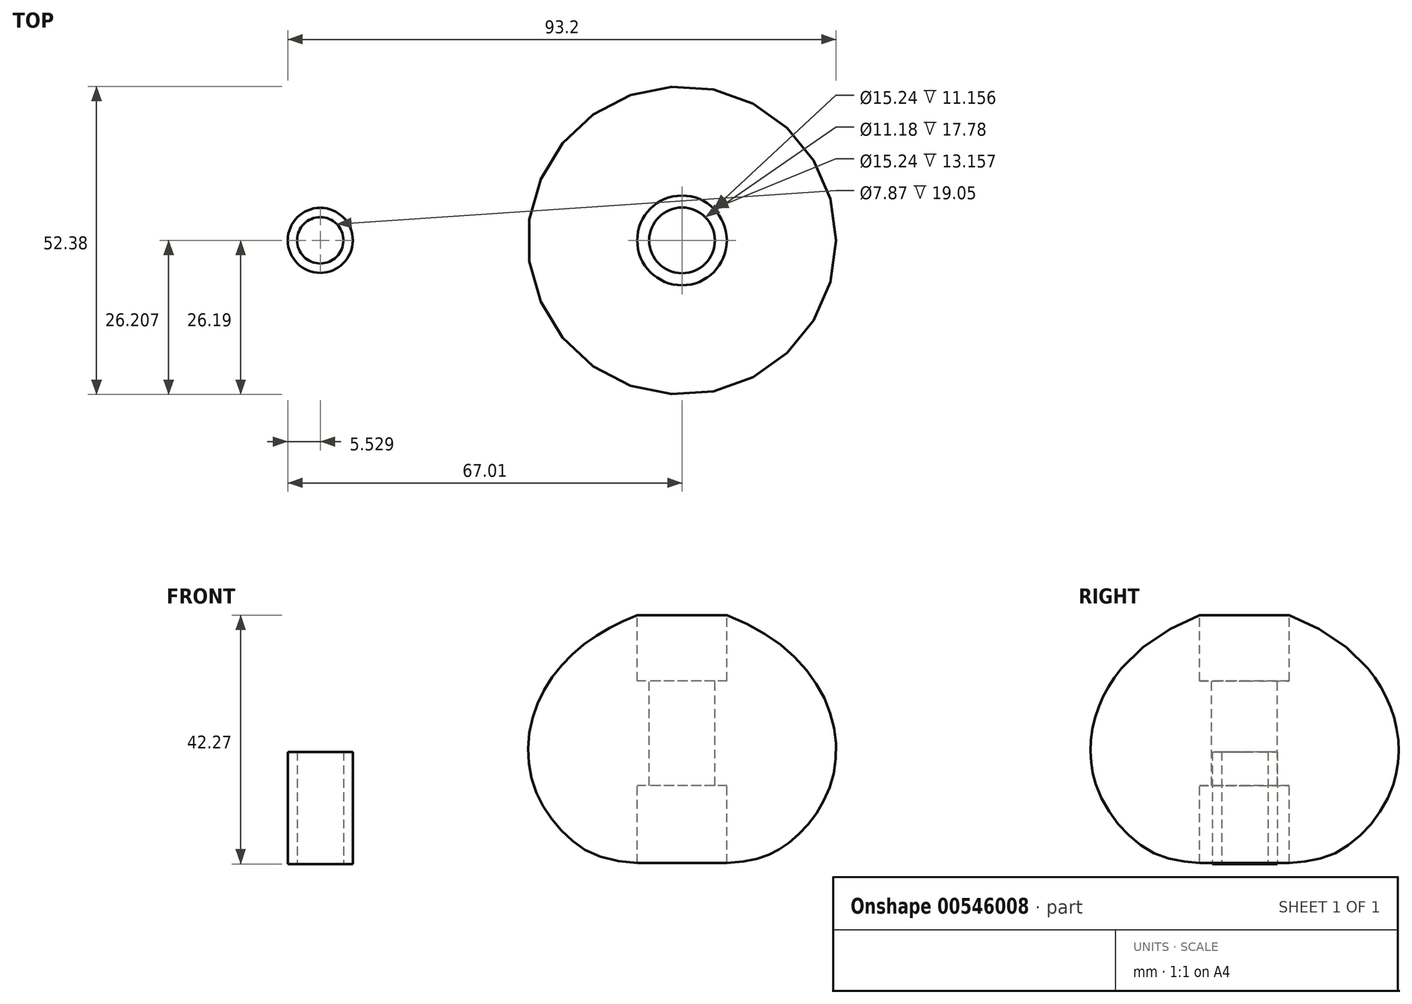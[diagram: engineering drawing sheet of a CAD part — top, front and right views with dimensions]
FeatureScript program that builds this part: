
annotation { "Feature Type Name" : "Feature", "Feature Type Description" : "" }
export const myFeature = defineFeature(function(context is Context, id is Id, definition is map)
    precondition{}
    {
        {
            var Q0;
            Q0=qCreatedBy(makeId("Top.planeOp"),FACE);
            var sketch = newSketch(context, id + "F0", { "sketchPlane" : qUnion([Q0])});
            skCircle(sketch, "E0", {"center": v(-115.86, 6.7) * mm, "radius": 3.94 * mm});
            skCircle(sketch, "E1", {"center": v(-115.86, 6.7) * mm, "radius": 5.52 * mm});
            skSolve(sketch);
        }
        {
            var Q0;
            Q0 = qSketchRegion(id + "F0", true);
            extrude(context, id + "F1", {"entities" : qUnion([Q0]), "depth" : 19.05 * mm, "offsetDistance" : 25.4 * mm});
        }
        {
            var Q0;
            Q0=qCreatedBy(makeId("Front.planeOp"),FACE);
            var sketch = newSketch(context, id + "F2", { "sketchPlane" : qUnion([Q0])});
            skLineSegment(sketch, "E2", {"start": v(0, 73.45) * mm, "end": v(0, -45.84) * mm, "construction": true});
            skLineSegment(sketch, "E3", {"start": v(45.9, 22.23) * mm, "end": v(-52.24, 22.22) * mm, "construction": true});
            skLineSegment(sketch, "E4.MirrorCS", {"start": v(5.59, 13.33) * mm, "end": v(7.62, 13.33) * mm});
            skLineSegment(sketch, "E5.MirrorCS", {"start": v(7.62, 13.33) * mm, "end": v(7.62, 0.18) * mm});
            skLineSegment(sketch, "E6.MirrorCS", {"start": v(7.62, 31.11) * mm, "end": v(7.62, 42.27) * mm});
            skFitSpline(sketch, "E7.MirrorCS", {"points": [v(0, 44.45) * mm, v(23.26, 29.9) * mm, v(25.4, 13.92) * mm, v(17.55, 3.12) * mm, v(0, 0) * mm], "startDerivative": vector(114.18, -23.1) * mm, "endDerivative": vector(-122.97, 0) * mm});
            skLineSegment(sketch, "E8.MirrorCS", {"start": v(0, -29) * mm, "end": v(0, 90.3) * mm, "construction": true});
            skLineSegment(sketch, "E9.MirrorCS", {"start": v(5.59, 0.08) * mm, "end": v(5.59, 42.99) * mm});
            skLineSegment(sketch, "E10", {"start": v(7.62, 31.11) * mm, "end": v(5.59, 31.11) * mm});
            skSolve(sketch);
        }
        {
            var Q0;
            Q0=makeQuery(id+"F1.opExtrude","SWEPT_BODY",BODY,{"disambiguationData":[OSD([sQuery(id+"F0.wireOp",EDGE,"E0"),sQuery(id+"F0.wireOp",EDGE,"E1")])]});
            transform(context, id + "F3", {"entities" : qUnion([Q0]), "transformType" : TransformType.TRANSLATION_3D, "dx" : 54.38 * mm, "dy" : -6.68 * mm, "dz" : 0 * mm, "makeCopy" : false});
        }
        {
            var Q0;
            {var subQ1=sQuery(id+"F2.wireOp",EDGE,"is7WIAhI-uB1y-75Ek-9FhK-P4BjWs5Zj6hR");Q0=makeQuery(id+"F2.imprint","IMPRINT",FACE,{"disambiguationData":[TD([[makeQuery(id+"F2.imprint","IMPRINT",EDGE,{"derivedFrom":subQ1}),-1.0]])]});}
            var Q1;
            {var subQ3=sQuery(id+"F2.wireOp",EDGE,"E4.MirrorCS");Q1=makeQuery(id+"F2.imprint","IMPRINT",FACE,{"disambiguationData":[TD([[makeQuery(id+"F2.imprint","IMPRINT",EDGE,{"derivedFrom":subQ3}),1.0]])]});}
            var Q2;
            Q2=sQuery(id+"F2.wireOp",EDGE,"E2");
            revolve(context, id + "F4", {"entities" : qUnion([Q0, Q1]), "axis" : qUnion([Q2]), "revolveType" : RevolveType.FULL});
        }
    });
